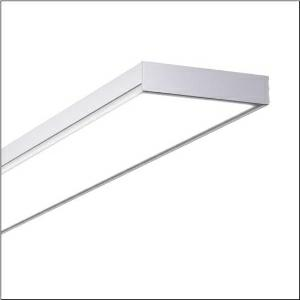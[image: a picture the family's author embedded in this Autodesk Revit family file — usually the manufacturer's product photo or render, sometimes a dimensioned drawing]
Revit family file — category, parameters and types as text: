
# Revit family: apollon_r__31_surface_51mp25wd2441e_f457
name_source: partatom
category: Lighting Fixtures
units: mm (PartAtom-declared; Revit-internal decimal feet)

## family parameters
Cut with Voids When Loaded = No
Host = Face
Light Source = No
Part Type = Normal
Room Calculation Point = No
Round Connector Dimension = Use Diameter
Shared = No

## types (1)
- Apollon® 31 Surface (1 x LED, 3800 lm, 28 W, 4000K)
    Apparent Load = 28 VA
    CIE Flux Codes = 61 87 97 97 100
    Color Rendering = 80
    Color Temperature = 4000K
    Default Elevation = 1800 mm
    Description = Apollon® 31 Surface, office luminaire, primary optical cover: micro prismatic cover, of PMMA, light emission: direct distribution, primary light characteristic: symmetric, installation type: surface-mounted, LED, rated luminous flux: 3.800lm, luminous efficacy: 134lm/W, light colour: 840, colour temperature: 4000K, control gear: DALI 2, with terminal, 5-pole, mains connection: 220..240V, AC, 50/60Hz, rated input power: 28W, housing, of sheet steel, coil coated, metallic grey (RAL 9006), length: 1.245mm, width: 200mm, height: 44mm, protection rating (complete): IP20, insulation class (complete): insulation class II (safety insulation), certification: CE, impact resistance: IK02, permissible operating ambient temperature: -20..+40°C, standard: EN 60598-2-22, packaging unit: 1 piece
    Height = 44 mm
    Lamp = 1 x LED
    Lamp Light Flux = 3800 lm
    Lamp Power = 28 W
    Lamp count = 1
    Length = 1245 mm
    Luminous efficacy = 136 lm/W
    Manufacturer = Siteco
    ModVariant = No
    Model = 51MP25WD2441E
    Mounting Place = Ceiling
    Mounting Type = Surface mounted
    Number of Poles = 1
    OnlyDefault = Yes
    Power Factor = 1
    Product Name = Apollon® 31 Surface
    Product group = office luminaire | ceiling mounted
    ProductGroupID = 303
    Protection Class = Protection class II
    Protection Degree = IP 20
    RLX_Detail_Level = 1
    RLX_Emergency_Light_Flux = 0 lm
    RLX_Emergency_Type = 0
    RLX_Emergency_Type_DB = No
    RlxData = <blob elided: 24105 chars, md5=062ba8bd>
    Socket = socket
    Standby Power = 0 W
    System Light Flux = 3800 lm
    System Power = 28 W
    Type Comments = Product without accessories
    Type Image = l_1313654.jpg
    URL = http://relux.com
    VarID = ---
    Voltage = 0 V
    Weight = 0.00 kg
    Width = 200 mm  [stored 0.656168 ft]

note: [stored X ft] marks values corroborated as IEEE doubles in the binary element streams (Revit-internal decimal feet)

## geometry (parser evidence)
native form markers: Blend x4, Sweep x10
no freeform markers — native parametric forms only
